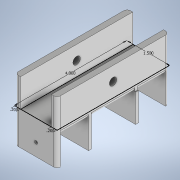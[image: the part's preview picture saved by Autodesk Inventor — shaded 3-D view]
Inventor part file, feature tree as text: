
AUTODESK INVENTOR PART (.ipt)
format: ipt  version: 2020 (Build 240168000, 168)  size: 192,000 bytes
history: native  units: in
note: dims shown in document units (in); Inventor stores cm internally (conversion verified against a paired STEP export)
features: sketch x3, extrude x3, hole x2, fillet x1
ambient origin geometry x8: Origin, YZ Plane, XZ Plane, XY Plane, X Axis, Y Axis, Z Axis, Center Point
bodies: Solid1 (feature_tree)
feature tree (9):
  sketch  "Sketch1"  dims[d0=1.5in d1=4.0in]
  extrude  "Extrusion1"  Depth=4.0in
  extrude  "Extrusion2"  Depth=0.2in
  hole  "Hole1"  [1 undecoded]
  extrude  "Extrusion3"  Depth=0.1in
  hole  "Hole2"  [1 undecoded]
  fillet  "Fillet1"  Radius=1.0in
  sketch  "Sketch2"  dims[d2=0.2in d3=0.2in]
  sketch  "Sketch3"  dims[d4=1.0in d5=0.0in d6=0.2in d7=0.0in d8=0.5in d9=0.266in d10=0.75in d11=0.438in d12=0.25in d13=0.5635in d14=1.0in d15=0.8108in d16=0.5in d17=1.0in d18=0.75in d19=0.125in d20=0.125in d21=1.0in d22=0.0in d23=0.45in d24=0.1125in d25=0.75in d26=0.438in d27=0.25in d28=0.5635in d29=1.0in d30=0.8108in d31=0.125in d32=0.125in d33=0.125in d34=1.0in d35=1.0in d36=90.0deg d37=0.1in d38=0.1in]
note: 2 required parameter values undecoded (feature->parameter linkage not recoverable at this tier; creation-order binding heuristic only, values carry confidence <= 0.55)
